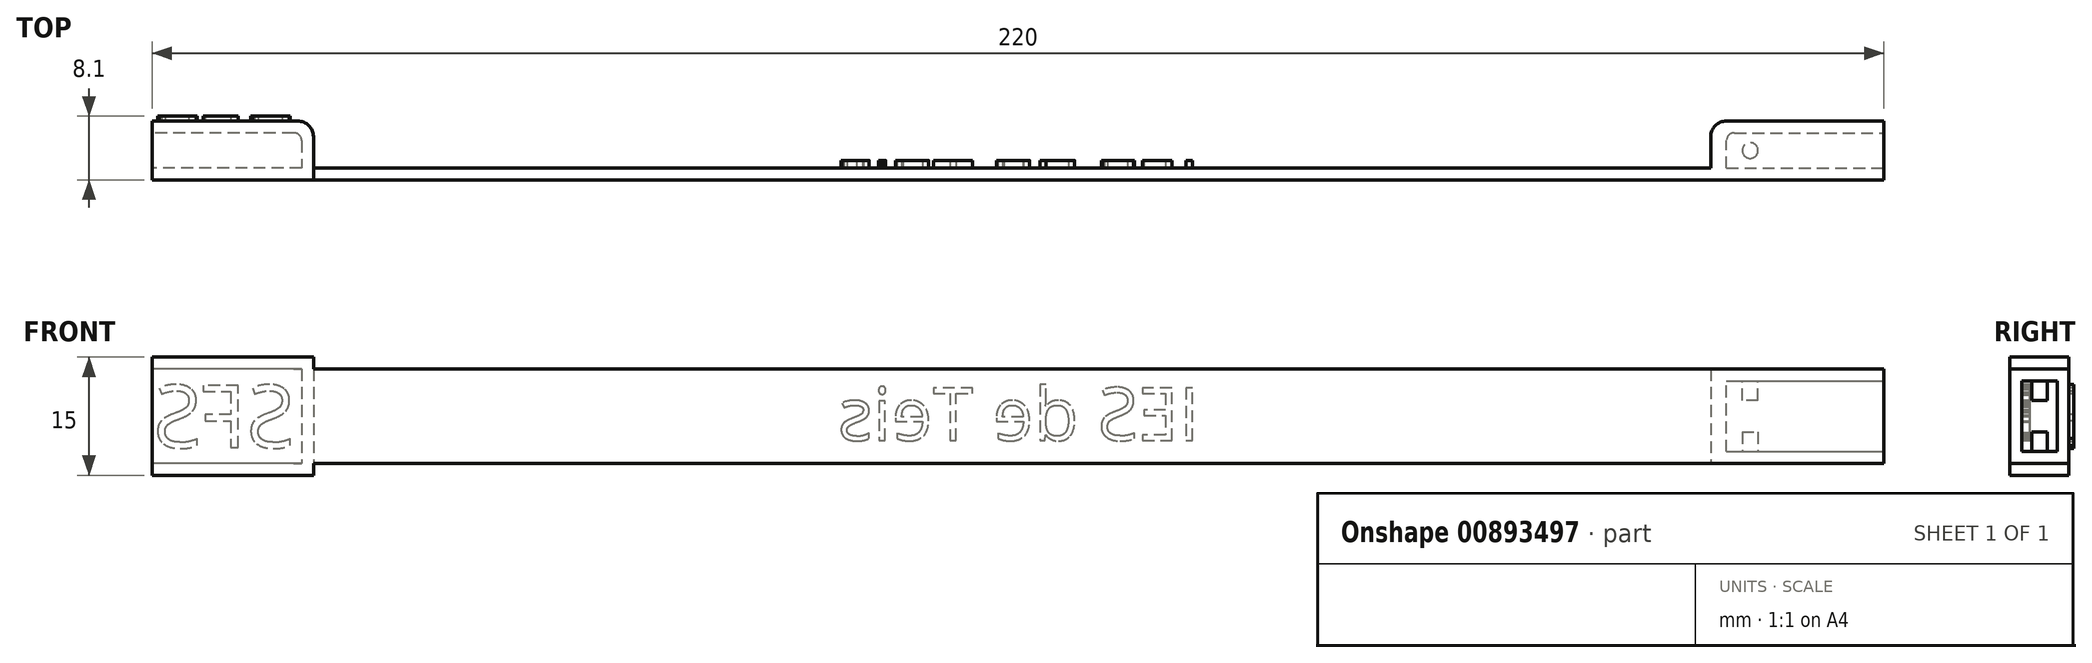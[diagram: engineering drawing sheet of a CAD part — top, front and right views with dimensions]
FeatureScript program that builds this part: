
annotation { "Feature Type Name" : "Feature", "Feature Type Description" : "" }
export const myFeature = defineFeature(function(context is Context, id is Id, definition is map)
    precondition{}
    {
        {
            var Q0;
            Q0=qCreatedBy(makeId("Front.planeOp"),FACE);
            var sketch = newSketch(context, id + "F0", { "sketchPlane" : qUnion([Q0])});
            skLineSegment(sketch, "E0.bottom", {"start": v(-100, 0) * mm, "end": v(100, 0) * mm});
            skLineSegment(sketch, "E0.top", {"start": v(-100, 12) * mm, "end": v(100, 12) * mm});
            skLineSegment(sketch, "E0.left", {"start": v(-100, 0) * mm, "end": v(-100, 12) * mm});
            skLineSegment(sketch, "E0.right", {"start": v(100, 0) * mm, "end": v(100, 12) * mm});
            skSolve(sketch);
        }
        {
            var Q0;
            Q0=qCreatedBy(makeId("Right.planeOp"),FACE);
            cPlane(context, id + "F1", {"entities" : qUnion([Q0]), "cplaneType" : CPlaneType.OFFSET, "offset" : 110 * mm, "width" : 150 * mm, "height" : 150 * mm});
        }
        {
            var Q0;
            Q0=qCreatedBy(makeId("Right.planeOp"),FACE);
            cPlane(context, id + "F2", {"entities" : qUnion([Q0]), "cplaneType" : CPlaneType.OFFSET, "offset" : 110 * mm, "oppositeDirection" : true, "width" : 150 * mm, "height" : 150 * mm});
        }
        {
            var Q0;
            Q0=qCreatedBy(id+"F1.planeOp",FACE);
            var sketch = newSketch(context, id + "F3", { "sketchPlane" : qUnion([Q0])});
            skLineSegment(sketch, "E1.bottom", {"start": v(0, 0) * mm, "end": v(7.5, 0) * mm});
            skLineSegment(sketch, "E1.top", {"start": v(0, 12) * mm, "end": v(7.5, 12) * mm});
            skLineSegment(sketch, "E1.left", {"start": v(0, 0) * mm, "end": v(0, 12) * mm});
            skLineSegment(sketch, "E1.right", {"start": v(7.5, 0) * mm, "end": v(7.5, 12) * mm});
            skSolve(sketch);
        }
        {
            var Q0;
            Q0=qCreatedBy(id+"F2.planeOp",FACE);
            var sketch = newSketch(context, id + "F4", { "sketchPlane" : qUnion([Q0])});
            skLineSegment(sketch, "E2.bottom", {"start": v(7.5, -1.5) * mm, "end": v(0, -1.5) * mm});
            skLineSegment(sketch, "E2.top", {"start": v(7.5, 13.5) * mm, "end": v(0, 13.5) * mm});
            skLineSegment(sketch, "E2.left", {"start": v(7.5, -1.5) * mm, "end": v(7.5, 13.5) * mm});
            skPoint(sketch, "E3", {"position": v(0, -1.5) * mm});
            skLineSegment(sketch, "E4", {"start": v(0, 13.5) * mm, "end": v(0, -1.5) * mm});
            skSolve(sketch);
        }
        {
            var Q0;
            Q0=makeQuery(id+"F3.imprint","IMPRINT",FACE,{"disambiguationData":[TD([[makeQuery(id+"F3.imprint","IMPRINT",EDGE,{"derivedFrom":sQuery(id+"F3.wireOp",EDGE,"E1.bottom")}),1.0]])]});
            extrude(context, id + "F5", {"entities" : qUnion([Q0]), "oppositeDirection" : true, "depth" : 22 * mm, "offsetDistance" : 25 * mm});
        }
        {
            var Q0;
            Q0=qSketchRegion(id+"F4",true);
            var Q1;
            Q1=makeQuery(id+"F4.imprint","IMPRINT",FACE,{"disambiguationData":[TD([[makeQuery(id+"F4.imprint","IMPRINT",EDGE,{"derivedFrom":sQuery(id+"F4.wireOp",EDGE,"Hlka1Qad-GjJF-81ZI-ByxS-eIRTQnkwmmPv.bottom")}),1.0]])]});
            extrude(context, id + "F6", {"entities" : qUnion([Q0, Q1]), "depth" : 20.5 * mm, "offsetDistance" : 25 * mm});
        }
        {
            var Q0;
            Q0=qSketchRegion(id+"F0",true);
            extrude(context, id + "F7", {"entities" : qUnion([Q0]), "oppositeDirection" : true, "depth" : 1.5 * mm, "offsetDistance" : 25 * mm});
        }
        {
            var Q0;
            Q0=qCreatedBy(id+"F1.planeOp",FACE);
            var sketch = newSketch(context, id + "F8", { "sketchPlane" : qUnion([Q0])});
            skLineSegment(sketch, "E5.bottom", {"start": v(1.5, 1.5) * mm, "end": v(6, 1.5) * mm});
            skLineSegment(sketch, "E5.top", {"start": v(1.5, 10.5) * mm, "end": v(6, 10.5) * mm});
            skLineSegment(sketch, "E5.left", {"start": v(1.5, 1.5) * mm, "end": v(1.5, 10.5) * mm});
            skLineSegment(sketch, "E5.right", {"start": v(6, 1.5) * mm, "end": v(6, 10.5) * mm});
            skSolve(sketch);
        }
        {
            var Q0;
            Q0=qSketchRegion(id+"F8",true);
            extrude(context, id + "F9", {"entities" : qUnion([Q0]), "operationType" : NewBodyOperationType.REMOVE, "oppositeDirection" : true, "depth" : 20 * mm, "offsetDistance" : 25 * mm});
        }
        {
            var Q0;
            Q0=qCreatedBy(id+"F2.planeOp",FACE);
            var sketch = newSketch(context, id + "F10", { "sketchPlane" : qUnion([Q0])});
            skLineSegment(sketch, "E6.bottom", {"start": v(6, 0) * mm, "end": v(1.5, 0) * mm});
            skLineSegment(sketch, "E6.top", {"start": v(6, 12) * mm, "end": v(1.5, 12) * mm});
            skLineSegment(sketch, "E6.left", {"start": v(6, 0) * mm, "end": v(6, 12) * mm});
            skLineSegment(sketch, "E7", {"start": v(1.5, 12) * mm, "end": v(1.5, 0) * mm});
            skSolve(sketch);
        }
        {
            var Q0;
            Q0=qSketchRegion(id+"F10",true);
            var Q1;
            Q1 = qSketchRegion(id + "F12", true);
            extrude(context, id + "F11", {"entities" : qUnion([Q0, Q1]), "operationType" : NewBodyOperationType.REMOVE, "depth" : 19 * mm, "offsetDistance" : 25 * mm});
        }
        {
            var Q0;
            Q0=makeQuery(id+"F7.opExtrude","CAP_FACE",FACE,{"disambiguationData":[OSD([sQuery(id+"F0.wireOp",EDGE,"E0.bottom"),sQuery(id+"F0.wireOp",EDGE,"E0.top"),sQuery(id+"F0.wireOp",EDGE,"E0.left"),sQuery(id+"F0.wireOp",EDGE,"E0.right")])],"isStart":false});
            var sketch = newSketch(context, id + "F12", { "sketchPlane" : qUnion([Q0])});
            skText(sketch, "E8", { "text": "IES de Teis", "fontName": "OpenSans-Regular.ttf"});
            const initialGuessF12  = {"E8": [-0.02305, 0.00294, 1, 0, 0.00672]};
            skSetInitialGuess(sketch, initialGuessF12);
            skSolve(sketch);
        }
        {
            var Q0;
            Q0=qSketchRegion(id+"F12",true);
            extrude(context, id + "F13", {"entities" : qUnion([Q0]), "operationType" : NewBodyOperationType.ADD, "depth" : 1 * mm, "offsetDistance" : 25 * mm});
        }
        {
            var Q0;
            Q0=makeQuery(id+"F6.opExtrude","CAP_EDGE",EDGE,{"disambiguationData":[OSD([sQuery(id+"F4.wireOp",EDGE,"E2.left")])],"isStart":false});
            var Q1;
            Q1=makeQuery(id+"F5.opExtrude","CAP_EDGE",EDGE,{"disambiguationData":[OSD([sQuery(id+"F3.wireOp",EDGE,"E1.right")])],"isStart":false});
            fillet(context, id + "F14", {"entities" : qUnion([Q0, Q1]), "radius" : 2 * mm, "tangentPropagation" : true, "allowEdgeOverflow" : false});
        }
        {
            var Q0;
            Q0=makeQuery(id+"F5.opExtrude","SWEPT_BODY",BODY,{"disambiguationData":[OSD([sQuery(id+"F3.wireOp",EDGE,"E1.bottom"),sQuery(id+"F3.wireOp",EDGE,"E1.top"),sQuery(id+"F3.wireOp",EDGE,"E1.left"),sQuery(id+"F3.wireOp",EDGE,"E1.right")])]});
            var Q1;
            Q1=makeQuery(id+"F6.opExtrude","SWEPT_BODY",BODY,{"disambiguationData":[OSD([sQuery(id+"F4.wireOp",EDGE,"E2.bottom"),sQuery(id+"F4.wireOp",EDGE,"E2.top"),sQuery(id+"F4.wireOp",EDGE,"E2.left"),sQuery(id+"F4.wireOp",EDGE,"E2.right")])]});
            var Q2;
            Q2=makeQuery(id+"F7.opExtrude","SWEPT_BODY",BODY,{"disambiguationData":[OSD([sQuery(id+"F0.wireOp",EDGE,"E0.bottom"),sQuery(id+"F0.wireOp",EDGE,"E0.top"),sQuery(id+"F0.wireOp",EDGE,"E0.left"),sQuery(id+"F0.wireOp",EDGE,"E0.right")])]});
            booleanBodies(context, id + "F15", {"operationType" : BooleanOperationType.UNION, "tools" : qUnion([Q0, Q1, Q2])});
        }
        {
            var Q0;
            Q0=makeQuery(id+"F15.opBoolean","MERGE",FACE,{"derivedFrom":[makeQuery(id+"F7.opExtrude","SWEPT_FACE",FACE,{"disambiguationData":[OSD([sQuery(id+"F0.wireOp",EDGE,"E0.bottom")])]}),makeQuery(id+"F5.opExtrude","SWEPT_FACE",FACE,{"disambiguationData":[OSD([sQuery(id+"F3.wireOp",EDGE,"E1.bottom")])]})]});
            var sketch = newSketch(context, id + "F16", { "sketchPlane" : qUnion([Q0])});
            skPoint(sketch, "E9", {"position": v(93, -3.75) * mm});
            skCircle(sketch, "E10", {"center": v(93, -3.75) * mm, "radius": 1 * mm});
            skSolve(sketch);
        }
        {
            var Q0;
            Q0=makeQuery(id+"F16.imprint","IMPRINT",FACE,{"disambiguationData":[TD([[makeQuery(id+"F16.imprint","IMPRINT",EDGE,{"derivedFrom":sQuery(id+"F16.wireOp",EDGE,"E10")}),1.0]])]});
            extrude(context, id + "F17", {"entities" : qUnion([Q0]), "operationType" : NewBodyOperationType.ADD, "oppositeDirection" : true, "depth" : 4 * mm, "offsetDistance" : 25 * mm});
        }
        {
            var Q0;
            Q0=makeQuery(id+"F15.opBoolean","MERGE",FACE,{"derivedFrom":[makeQuery(id+"F7.opExtrude","SWEPT_FACE",FACE,{"disambiguationData":[OSD([sQuery(id+"F0.wireOp",EDGE,"E0.top")])]}),makeQuery(id+"F5.opExtrude","SWEPT_FACE",FACE,{"disambiguationData":[OSD([sQuery(id+"F3.wireOp",EDGE,"E1.top")])]})]});
            var sketch = newSketch(context, id + "F18", { "sketchPlane" : qUnion([Q0])});
            skPoint(sketch, "E11", {"position": v(93, 3.75) * mm});
            skCircle(sketch, "E12", {"center": v(93, 3.75) * mm, "radius": 1 * mm});
            skSolve(sketch);
        }
        {
            var Q0;
            Q0=makeQuery(id+"F18.imprint","IMPRINT",FACE,{"disambiguationData":[TD([[makeQuery(id+"F18.imprint","IMPRINT",EDGE,{"derivedFrom":sQuery(id+"F18.wireOp",EDGE,"E12")}),1.0]])]});
            extrude(context, id + "F19", {"entities" : qUnion([Q0]), "operationType" : NewBodyOperationType.ADD, "oppositeDirection" : true, "depth" : 4 * mm, "offsetDistance" : 25 * mm});
        }
        {
            var Q0;
            Q0=makeQuery(id+"F9.boolean.opBoolean","COPY",EDGE,{"derivedFrom":makeQuery(id+"F9.opExtrude","CAP_EDGE",EDGE,{"disambiguationData":[OSD([sQuery(id+"F8.wireOp",EDGE,"E5.right")])],"isStart":false})});
            fillet(context, id + "F20", {"entities" : qUnion([Q0]), "radius" : 1 * mm, "tangentPropagation" : true, "allowEdgeOverflow" : false});
        }
        {
            var Q0;
            Q0=makeQuery(id+"F11.boolean.opBoolean","COPY",EDGE,{"derivedFrom":makeQuery(id+"F11.opExtrude","CAP_EDGE",EDGE,{"disambiguationData":[OSD([sQuery(id+"F10.wireOp",EDGE,"E6.left")])],"isStart":false})});
            fillet(context, id + "F21", {"entities" : qUnion([Q0]), "radius" : 1 * mm, "tangentPropagation" : true, "allowEdgeOverflow" : false});
        }
        {
            var Q0;
            Q0=makeQuery(id+"F6.opExtrude","SWEPT_FACE",FACE,{"disambiguationData":[OSD([sQuery(id+"F4.wireOp",EDGE,"E2.left")])]});
            var sketch = newSketch(context, id + "F22", { "sketchPlane" : qUnion([Q0])});
            skText(sketch, "E13", { "text": "SFS", "fontName": "OpenSans-Regular.ttf"});
            const initialGuessF22  = {"E13": [0.09188, 0.002, 1, 0, 0.008]};
            skSetInitialGuess(sketch, initialGuessF22);
            skSolve(sketch);
        }
        {
            var Q0;
            Q0 = qSketchRegion(id + "F22", true);
            extrude(context, id + "F23", {"entities" : qUnion([Q0]), "operationType" : NewBodyOperationType.ADD, "depth" : 0.6 * mm, "offsetDistance" : 25 * mm});
        }
    });
